annotation { "Feature Type Name" : "Feature", "Feature Type Description" : "" }
export const myFeature = defineFeature(function(context is Context, id is Id, definition is map)
    precondition{}
    {
        {
            var Q0;
            Q0=qCreatedBy(makeId("Top.planeOp"),FACE);
            var sketch = newSketch(context, id + "F0", { "sketchPlane" : qUnion([Q0])});
            skEllipse(sketch, "E0", {"center": v(0, 0) * mm, "majorRadius": 53.97 * mm, "minorRadius": 34.93 * mm, "majorAxis": v(-1, 0)});
            skSolve(sketch);
        }
        {
            var Q0;
            Q0 = qSketchRegion(id + "F0", true);
            extrude(context, id + "F1", {"entities" : qUnion([Q0]), "depth" : 2.54 * mm});
        }
        {
            var Q0;
            Q0=makeQuery(id+"F1.opExtrude","CAP_FACE",FACE,{"disambiguationData":[OSD([sQuery(id+"F0.wireOp",EDGE,"E0")])],"isStart":false});
            var sketch = newSketch(context, id + "F2", { "sketchPlane" : qUnion([Q0])});
            skEllipse(sketch, "E1", {"center": v(0, 0) * mm, "majorRadius": 50.8 * mm, "minorRadius": 31.75 * mm, "majorAxis": v(1, 0), "construction": true});
            skText(sketch, "E2", { "text": "FCUMC", "fontName": "OpenSans-Regular.ttf"});
            skText(sketch, "E3", { "text": "YOUTH", "fontName": "AllertaStencil-Regular.ttf"});
            skText(sketch, "E4", { "text": "Choir Tour", "fontName": "AllertaStencil-Regular.ttf"});
            skText(sketch, "E5", { "text": "2016", "fontName": "AllertaStencil-Regular.ttf"});
            skPoint(sketch, "E6", {"position": v(0, -31.75) * mm});
            skLineSegment(sketch, "E7", {"start": v(0, 11.5) * mm, "end": v(0, 10.02) * mm, "construction": true});
            skLineSegment(sketch, "E8", {"start": v(0, -10.02) * mm, "end": v(0, -11.5) * mm, "construction": true});
            skLineSegment(sketch, "E9", {"start": v(0, -18.39) * mm, "end": v(0, -19.87) * mm, "construction": true});
            const initialGuessF2  = {"E2": [-0.03175, 0.0115, 1, 0, 0.01328], "E3": [-0.0482, -0.01002, 1, 0, 0.02004], "E4": [-0.0251, -0.01839, 1, 0, 0.00688], "E5": [-0.01648, -0.03003, 1, 0, 0.01016]};
            skSetInitialGuess(sketch, initialGuessF2);
            skSolve(sketch);
        }
        {
            var Q0;
            Q0 = qSketchRegion(id + "F2", true);
            var Q1;
            Q1=makeQuery(id+"F1.opExtrude","CAP_FACE",FACE,{"disambiguationData":[OSD([sQuery(id+"F0.wireOp",EDGE,"E0")])],"isStart":true});
            extrude(context, id + "F3", {"entities" : qUnion([Q0]), "operationType" : NewBodyOperationType.REMOVE, "endBound" : BoundingType.UP_TO_SURFACE, "oppositeDirection" : true, "endBoundEntityFace" : qUnion([Q1]), "depth" : 1.27 * mm});
        }
        {
            var Q0;
            Q0=makeQuery(id+"F1.opExtrude","CAP_FACE",FACE,{"disambiguationData":[OSD([sQuery(id+"F0.wireOp",EDGE,"E0")])],"isStart":true});
            var sketch = newSketch(context, id + "F4", { "sketchPlane" : qUnion([Q0])});
            skLineSegment(sketch, "E10", {"start": v(-53.97, 0) * mm, "end": v(0, 0) * mm, "construction": true});
            skEllipticalArc(sketch, "E11", {});
            skLineSegment(sketch, "E12", {"start": v(0, 0) * mm, "end": v(53.97, 0) * mm, "construction": true});
            skLineSegment(sketch, "E13", {"start": v(0, 0) * mm, "end": v(0, -34.93) * mm, "construction": true});
            skLineSegment(sketch, "E14", {"start": v(0, 0) * mm, "end": v(0, 34.93) * mm, "construction": true});
            skFitSpline(sketch, "E15.0", {"points": [v(-50.76, 1.5) * mm, v(-50.82, 0) * mm, v(-50.76, -1.5) * mm, v(-50.53, -3.47) * mm, v(-49.97, -5.91) * mm, v(-48.84, -8.82) * mm, v(-47.27, -11.67) * mm, v(-45.24, -14.44) * mm, v(-42.77, -17.12) * mm, v(-40.34, -19.24) * mm, v(-38.18, -20.86) * mm, v(-36.46, -22.04) * mm, v(-34.63, -23.16) * mm, v(-32.1, -24.57) * mm, v(-28.73, -26.19) * mm, v(-24.42, -27.86) * mm, v(-19.87, -29.25) * mm, v(-15.11, -30.35) * mm, v(-10.2, -31.15) * mm, v(-5.99, -31.56) * mm, v(-2.58, -31.72) * mm, v(0, -31.76) * mm, v(2.58, -31.72) * mm, v(5.99, -31.56) * mm, v(10.2, -31.15) * mm, v(15.11, -30.35) * mm, v(19.87, -29.25) * mm, v(24.42, -27.86) * mm, v(28.73, -26.19) * mm, v(32.1, -24.57) * mm, v(34.63, -23.16) * mm, v(36.46, -22.04) * mm, v(38.18, -20.86) * mm, v(40.34, -19.24) * mm, v(42.77, -17.12) * mm, v(45.24, -14.44) * mm, v(47.27, -11.67) * mm, v(48.84, -8.82) * mm, v(49.97, -5.91) * mm, v(50.53, -3.47) * mm, v(50.76, -1.5) * mm, v(50.82, 0) * mm, v(50.76, 1.5) * mm, v(50.53, 3.47) * mm, v(49.97, 5.91) * mm, v(48.84, 8.82) * mm, v(47.27, 11.67) * mm, v(45.24, 14.44) * mm, v(42.77, 17.12) * mm, v(40.34, 19.24) * mm, v(38.18, 20.86) * mm, v(36.46, 22.04) * mm, v(34.63, 23.16) * mm, v(32.1, 24.57) * mm, v(28.73, 26.19) * mm, v(24.42, 27.86) * mm, v(19.87, 29.25) * mm, v(15.11, 30.35) * mm, v(10.2, 31.15) * mm, v(5.99, 31.56) * mm, v(2.58, 31.72) * mm, v(0, 31.76) * mm, v(-2.58, 31.72) * mm, v(-5.99, 31.56) * mm, v(-10.2, 31.15) * mm, v(-15.11, 30.35) * mm, v(-19.87, 29.25) * mm, v(-24.42, 27.86) * mm, v(-28.73, 26.19) * mm, v(-32.1, 24.57) * mm, v(-34.63, 23.16) * mm, v(-36.46, 22.04) * mm, v(-38.18, 20.86) * mm, v(-40.34, 19.24) * mm, v(-42.77, 17.12) * mm, v(-45.24, 14.44) * mm, v(-47.27, 11.67) * mm, v(-48.84, 8.82) * mm, v(-49.97, 5.91) * mm, v(-50.53, 3.47) * mm, v(-50.76, 1.5) * mm, v(-50.82, 0) * mm, v(-50.76, -1.5) * mm, v(-50.76, 1.5) * mm]});
            skArc(sketch, "E16", {"start": v(-3.17, -34.86) * mm, "mid": v(0, -38.1) * mm, "end": v(3.17, -34.86) * mm});
            skArc(sketch, "E17", {"start": v(-5.71, -34.73) * mm, "mid": v(0, -40.64) * mm, "end": v(5.71, -34.73) * mm});
            skLineSegment(sketch, "E18", {"start": v(0, -38.1) * mm, "end": v(0, -40.64) * mm, "construction": true});
            skLineSegment(sketch, "E19.trimOffspring", {"start": v(4.66, -31.61) * mm, "end": v(4.66, -31.61) * mm});
            skArc(sketch, "E20", {"start": v(-3.17, -34.86) * mm, "mid": v(0, -34.92) * mm, "end": v(3.17, -34.86) * mm});
            const initialGuessF4  = {"E11": [0, 0, -1, 0, 0.053975, 0.034925, 1.676814827878772, 1.464777825711021]};
            skSetInitialGuess(sketch, initialGuessF4);
            skSolve(sketch);
        }
        {
            var Q0;
            Q0 = qSketchRegion(id + "F4", true);
            var Q1;
            Q1=makeQuery(id+"F1.opExtrude","CAP_FACE",FACE,{"disambiguationData":[OSD([sQuery(id+"F0.wireOp",EDGE,"E0")])],"isStart":false});
            extrude(context, id + "F5", {"entities" : qUnion([Q0]), "operationType" : NewBodyOperationType.ADD, "endBound" : BoundingType.UP_TO_SURFACE, "oppositeDirection" : true, "endBoundEntityFace" : qUnion([Q1]), "depth" : 25.4 * mm});
        }
    });